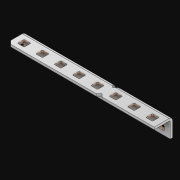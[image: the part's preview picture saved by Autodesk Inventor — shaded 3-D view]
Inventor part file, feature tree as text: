
AUTODESK INVENTOR PART (.ipt)
format: ipt  version: 2021 (Build 250183000, 183)  size: 597,504 bytes
history: native  units: in
note: dims shown in document units (in); Inventor stores cm internally (conversion verified against a paired STEP export)
features: extrude x17, other x16, sketch x3, pattern_linear x1, sheet_metal_op x1
ambient origin geometry x8: Origin, YZ Plane, XZ Plane, XY Plane, X Axis, Y Axis, Z Axis, Center Point
bodies: Solid1 (feature_tree)
feature tree (38):
  pattern_linear  "Rectangular Pattern1"  Spacing1=0.063in  [1 undecoded]
  extrude  "Extrusion1"  Depth=0.5in
  sketch  "Sketch1"  dims[d0=0.182in]
  other  "Srf1"
  sketch  "Sketch2"  dims[d1=0.063in d2=0.0in]
  other  "Srf2"
  other  "Srf3"
  other  "Srf5"
  other  "Srf7"
  other  "Srf9"
  other  "Srf11"
  other  "Srf13"
  other  "Srf15"
  other  "Srf4"
  other  "Srf6"
  other  "Srf8"
  other  "Srf10"
  other  "Srf12"
  other  "Srf14"
  other  "Srf16"
  sketch  "Sketch3"  dims[d3=0.182in d4=0.063in d5=0.0in d8=0.5in d9=13.5in d10=0.0in]
  sheet_metal_op  "Fold1"
  extrude  "ExtrusionSrf1"  Depth=0.5in TaperAngle=0.0deg
  extrude  "ExtrusionSrf2"  [1 undecoded]
  extrude  "ExtrusionSrf3"  [1 undecoded]
  extrude  "ExtrusionSrf4"  [1 undecoded]
  extrude  "ExtrusionSrf5"  [1 undecoded]
  extrude  "ExtrusionSrf6"  [1 undecoded]
  extrude  "ExtrusionSrf7"  [1 undecoded]
  extrude  "ExtrusionSrf8"  [1 undecoded]
  extrude  "ExtrusionSrf9"  [1 undecoded]
  extrude  "ExtrusionSrf37"  [1 undecoded]
  extrude  "ExtrusionSrf38"  [1 undecoded]
  extrude  "ExtrusionSrf39"  [1 undecoded]
  extrude  "ExtrusionSrf40"  [1 undecoded]
  extrude  "ExtrusionSrf41"  [1 undecoded]
  extrude  "ExtrusionSrf42"  [1 undecoded]
  extrude  "ExtrusionSrf43"  [1 undecoded]
note: 16 required parameter values undecoded (feature->parameter linkage not recoverable at this tier; creation-order binding heuristic only, values carry confidence <= 0.55)
